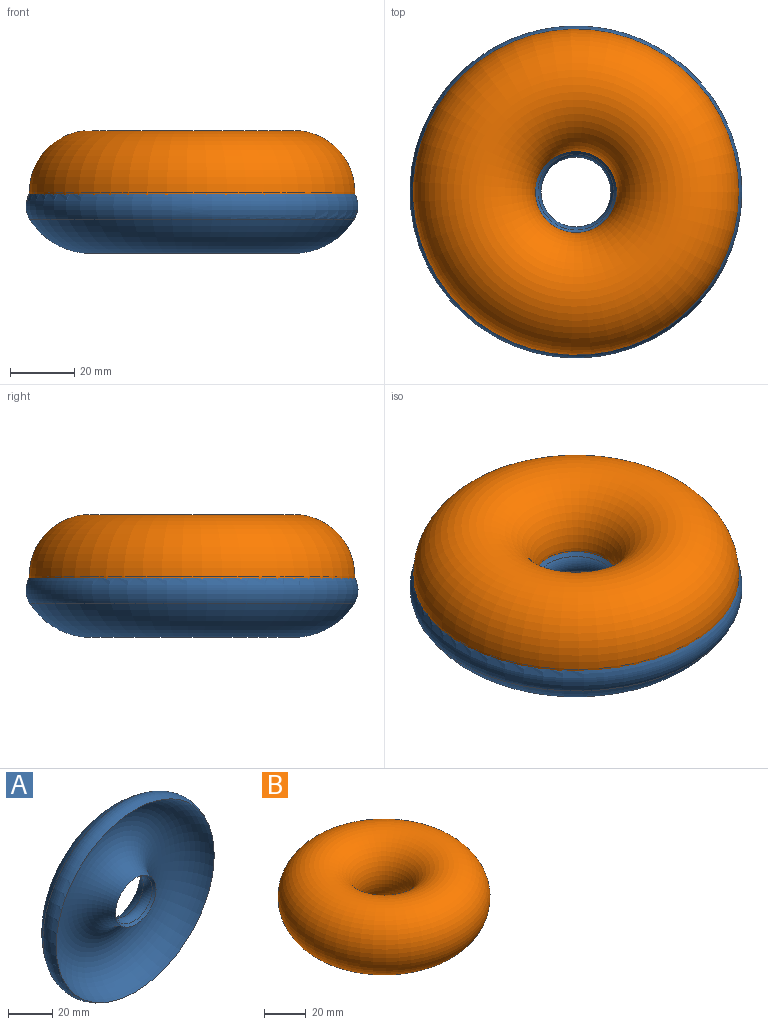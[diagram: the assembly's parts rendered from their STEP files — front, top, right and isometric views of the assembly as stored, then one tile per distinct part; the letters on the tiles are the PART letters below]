
ASSEMBLY  parts=2 mates=1
PART A: 5 faces, bbox 116.8x22.4x116.8 mm
  f0: torus R=31.75mm, axis (0,1,0), area 10654.4mm2, adj f2,f3
  f1: torus R=31.58mm, axis (0,1,0), area 9246.2mm2, adj f3,f4
  f2: cone r=15.05mm half-angle=36.2deg, axis (0,-1,0), area 135.6mm2, adj f0,f4
  f3: torus R=44.17mm, axis (0,-1,0), area 2793.4mm2, adj f0,f1
  f4: torus R=15.99mm, axis (0,1,0), area 385.5mm2, adj f1,f2
PART B: 1 faces, bbox 110x110x38.1 mm
  f0: torus R=31.75mm, axis (0,0,1), area 23878mm2
PLACE A rot(axis=(-1,0,0),90deg) t=(-0.51,0.51,1.93)mm
PLACE B t=(-0.51,0.51,-0.97)mm fixed
MATE parallel B.f0 <-> A.f0  axis (0,0,1) through (-0.51,0.51,-0.97)mm
